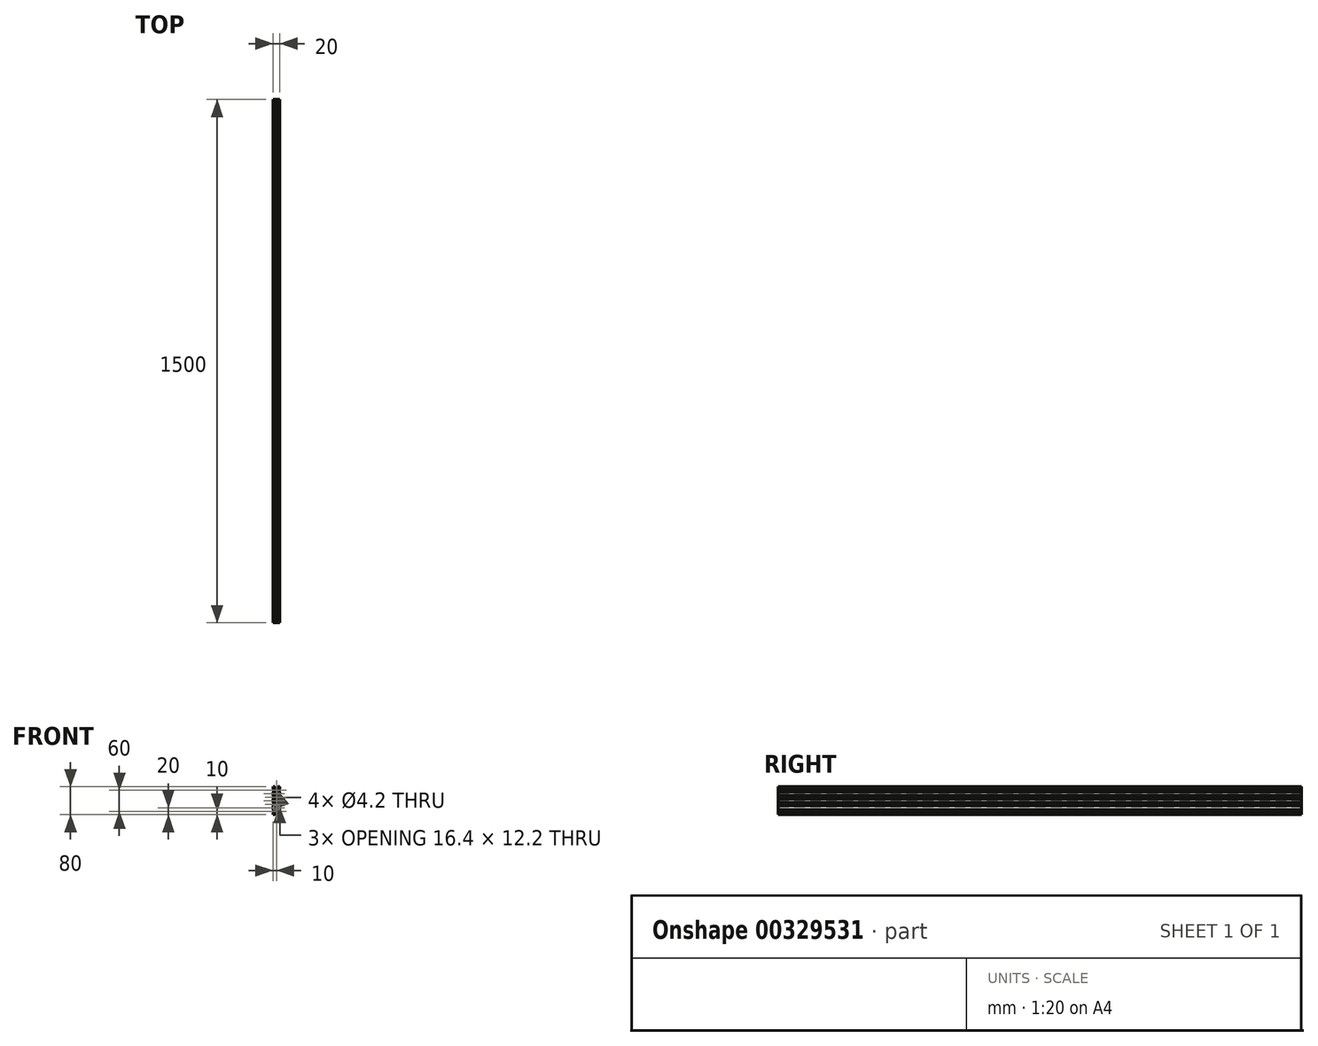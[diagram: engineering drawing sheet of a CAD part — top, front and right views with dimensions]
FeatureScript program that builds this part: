
annotation { "Feature Type Name" : "Feature", "Feature Type Description" : "" }
export const myFeature = defineFeature(function(context is Context, id is Id, definition is map)
    precondition{}
    {
        {
            var Q0;
            Q0=qCreatedBy(makeId("Front.planeOp"),FACE);
            var sketch = newSketch(context, id + "F0", { "sketchPlane" : qUnion([Q0])});
            skCircle(sketch, "E0", {"center": v(0, -30) * mm, "radius": 2.1 * mm});
            skCircle(sketch, "E1", {"center": v(0, -10) * mm, "radius": 2.1 * mm});
            skCircle(sketch, "E2", {"center": v(0, 10) * mm, "radius": 2.1 * mm});
            skCircle(sketch, "E3", {"center": v(0, 30) * mm, "radius": 2.1 * mm});
            skLineSegment(sketch, "E4.bottom", {"start": v(-10, 40) * mm, "end": v(-4.58, 40) * mm});
            skLineSegment(sketch, "E4.top", {"start": v(-10, -40) * mm, "end": v(-4.58, -40) * mm});
            skLineSegment(sketch, "E4.left", {"start": v(-10, 40) * mm, "end": v(-10, 34.58) * mm});
            skLineSegment(sketch, "E4.right", {"start": v(10, 40) * mm, "end": v(10, 34.58) * mm});
            skLineSegment(sketch, "E5", {"start": v(4.58, 40) * mm, "end": v(3.13, 38.2) * mm});
            skLineSegment(sketch, "E6", {"start": v(3.12, 38.2) * mm, "end": v(5.5, 38.2) * mm});
            skLineSegment(sketch, "E7", {"start": v(5.5, 38.2) * mm, "end": v(5.5, 36.56) * mm});
            skLineSegment(sketch, "E8", {"start": v(5.5, 36.56) * mm, "end": v(2.84, 33.9) * mm});
            skLineSegment(sketch, "E9", {"start": v(2.84, 33.9) * mm, "end": v(-2.84, 33.9) * mm});
            skLineSegment(sketch, "E10", {"start": v(-2.84, 33.9) * mm, "end": v(-5.5, 36.56) * mm});
            skLineSegment(sketch, "E11", {"start": v(-5.5, 36.56) * mm, "end": v(-5.5, 38.2) * mm});
            skLineSegment(sketch, "E12", {"start": v(-5.5, 38.2) * mm, "end": v(-3.12, 38.2) * mm});
            skLineSegment(sketch, "E13", {"start": v(-3.13, 38.2) * mm, "end": v(-4.58, 40) * mm});
            skLineSegment(sketch, "E14", {"start": v(0, 30) * mm, "end": v(-10, 40) * mm, "construction": true});
            skLineSegment(sketch, "E15", {"start": v(0, 30) * mm, "end": v(10, 40) * mm, "construction": true});
            skLineSegment(sketch, "E16.trimOffspring", {"start": v(4.58, 40) * mm, "end": v(10, 40) * mm});
            skLineSegment(sketch, "E17", {"start": v(-10, 34.58) * mm, "end": v(-8.2, 33.12) * mm});
            skLineSegment(sketch, "E18", {"start": v(-8.2, 33.12) * mm, "end": v(-8.2, 35.5) * mm});
            skLineSegment(sketch, "E19", {"start": v(-3.9, 32.84) * mm, "end": v(-3.9, 27.16) * mm});
            skLineSegment(sketch, "E20", {"start": v(-8.2, 24.5) * mm, "end": v(-8.2, 26.87) * mm});
            skLineSegment(sketch, "E21", {"start": v(-8.2, 26.88) * mm, "end": v(-10, 25.42) * mm});
            skLineSegment(sketch, "E22", {"start": v(-8.2, 35.5) * mm, "end": v(-6.56, 35.5) * mm});
            skLineSegment(sketch, "E23", {"start": v(-6.56, 35.5) * mm, "end": v(-3.9, 32.84) * mm});
            skLineSegment(sketch, "E24", {"start": v(-3.9, 27.16) * mm, "end": v(-6.56, 24.5) * mm});
            skLineSegment(sketch, "E25", {"start": v(-6.56, 24.5) * mm, "end": v(-8.2, 24.5) * mm});
            skPoint(sketch, "E26", {"position": v(-3.9, 30) * mm});
            skLineSegment(sketch, "E27.trimOffspring", {"start": v(-10, 25.42) * mm, "end": v(-10, 14.58) * mm});
            skLineSegment(sketch, "E28.0.1.0", {"start": v(-10, 14.58) * mm, "end": v(-8.2, 13.13) * mm});
            skLineSegment(sketch, "E28.0.1.1", {"start": v(-8.2, 13.13) * mm, "end": v(-8.2, 15.5) * mm});
            skLineSegment(sketch, "E28.0.1.2", {"start": v(-8.2, 15.5) * mm, "end": v(-6.56, 15.5) * mm});
            skLineSegment(sketch, "E28.0.1.3", {"start": v(-6.56, 15.5) * mm, "end": v(-3.9, 12.84) * mm});
            skLineSegment(sketch, "E28.0.1.4", {"start": v(-3.9, 12.84) * mm, "end": v(-3.9, 7.16) * mm});
            skLineSegment(sketch, "E28.0.1.5", {"start": v(-3.9, 7.16) * mm, "end": v(-6.56, 4.5) * mm});
            skLineSegment(sketch, "E28.0.1.6", {"start": v(-6.56, 4.5) * mm, "end": v(-8.2, 4.5) * mm});
            skLineSegment(sketch, "E28.0.1.7", {"start": v(-8.2, 4.5) * mm, "end": v(-8.2, 6.88) * mm});
            skLineSegment(sketch, "E28.0.1.8", {"start": v(-8.2, 6.88) * mm, "end": v(-10, 5.42) * mm});
            skLineSegment(sketch, "E28.0.2.0", {"start": v(-10, -5.42) * mm, "end": v(-8.2, -6.87) * mm});
            skLineSegment(sketch, "E28.0.2.1", {"start": v(-8.2, -6.87) * mm, "end": v(-8.2, -4.5) * mm});
            skLineSegment(sketch, "E28.0.2.2", {"start": v(-8.2, -4.5) * mm, "end": v(-6.56, -4.5) * mm});
            skLineSegment(sketch, "E28.0.2.3", {"start": v(-6.56, -4.5) * mm, "end": v(-3.9, -7.16) * mm});
            skLineSegment(sketch, "E28.0.2.4", {"start": v(-3.9, -7.16) * mm, "end": v(-3.9, -12.84) * mm});
            skLineSegment(sketch, "E28.0.2.5", {"start": v(-3.9, -12.84) * mm, "end": v(-6.56, -15.5) * mm});
            skLineSegment(sketch, "E28.0.2.6", {"start": v(-6.56, -15.5) * mm, "end": v(-8.2, -15.5) * mm});
            skLineSegment(sketch, "E28.0.2.7", {"start": v(-8.2, -15.5) * mm, "end": v(-8.2, -13.12) * mm});
            skLineSegment(sketch, "E28.0.2.8", {"start": v(-8.2, -13.12) * mm, "end": v(-10, -14.58) * mm});
            skLineSegment(sketch, "E28.0.3.0", {"start": v(-10, -25.42) * mm, "end": v(-8.2, -26.87) * mm});
            skLineSegment(sketch, "E28.0.3.1", {"start": v(-8.2, -26.87) * mm, "end": v(-8.2, -24.5) * mm});
            skLineSegment(sketch, "E28.0.3.2", {"start": v(-8.2, -24.5) * mm, "end": v(-6.56, -24.5) * mm});
            skLineSegment(sketch, "E28.0.3.3", {"start": v(-6.56, -24.5) * mm, "end": v(-3.9, -27.16) * mm});
            skLineSegment(sketch, "E28.0.3.4", {"start": v(-3.9, -27.16) * mm, "end": v(-3.9, -32.84) * mm});
            skLineSegment(sketch, "E28.0.3.5", {"start": v(-3.9, -32.84) * mm, "end": v(-6.56, -35.5) * mm});
            skLineSegment(sketch, "E28.0.3.6", {"start": v(-6.56, -35.5) * mm, "end": v(-8.2, -35.5) * mm});
            skLineSegment(sketch, "E28.0.3.7", {"start": v(-8.2, -35.5) * mm, "end": v(-8.2, -33.12) * mm});
            skLineSegment(sketch, "E28.0.3.8", {"start": v(-8.2, -33.12) * mm, "end": v(-10, -34.58) * mm});
            skLineSegment(sketch, "E28.direction1", {"start": v(-10, 34.58) * mm, "end": v(-10, 34.58) * mm});
            skLineSegment(sketch, "E28.direction2", {"start": v(-10, 34.58) * mm, "end": v(-10, 14.58) * mm, "construction": true});
            skLineSegment(sketch, "E29.trimOffspring", {"start": v(-10, 5.42) * mm, "end": v(-10, -5.42) * mm});
            skLineSegment(sketch, "E30.trimOffspring", {"start": v(-10, -14.58) * mm, "end": v(-10, -25.42) * mm});
            skLineSegment(sketch, "E31.trimOffspring", {"start": v(-10, -34.58) * mm, "end": v(-10, -40) * mm});
            skLineSegment(sketch, "E32", {"start": v(10, -25.42) * mm, "end": v(8.2, -26.87) * mm});
            skLineSegment(sketch, "E33", {"start": v(8.2, -26.87) * mm, "end": v(8.2, -24.5) * mm});
            skLineSegment(sketch, "E34", {"start": v(8.2, -24.5) * mm, "end": v(6.56, -24.5) * mm});
            skLineSegment(sketch, "E35", {"start": v(6.56, -24.5) * mm, "end": v(3.9, -27.16) * mm});
            skLineSegment(sketch, "E36", {"start": v(3.9, -27.16) * mm, "end": v(3.9, -32.84) * mm});
            skLineSegment(sketch, "E37", {"start": v(3.9, -32.84) * mm, "end": v(6.56, -35.5) * mm});
            skLineSegment(sketch, "E38", {"start": v(6.56, -35.5) * mm, "end": v(8.2, -35.5) * mm});
            skLineSegment(sketch, "E39", {"start": v(8.2, -35.5) * mm, "end": v(8.2, -33.12) * mm});
            skLineSegment(sketch, "E40", {"start": v(8.2, -33.12) * mm, "end": v(10, -34.58) * mm});
            skLineSegment(sketch, "E41.trimOffspring", {"start": v(10, -34.58) * mm, "end": v(10, -40) * mm});
            skLineSegment(sketch, "E42", {"start": v(-4.58, -40) * mm, "end": v(-3.12, -38.2) * mm});
            skLineSegment(sketch, "E43", {"start": v(-3.12, -38.2) * mm, "end": v(-5.5, -38.2) * mm});
            skLineSegment(sketch, "E44", {"start": v(-5.5, -38.2) * mm, "end": v(-5.5, -36.56) * mm});
            skLineSegment(sketch, "E45", {"start": v(-5.5, -36.56) * mm, "end": v(-2.84, -33.9) * mm});
            skLineSegment(sketch, "E46", {"start": v(-2.84, -33.9) * mm, "end": v(2.84, -33.9) * mm});
            skLineSegment(sketch, "E47", {"start": v(2.84, -33.9) * mm, "end": v(5.5, -36.56) * mm});
            skLineSegment(sketch, "E48", {"start": v(5.5, -36.56) * mm, "end": v(5.5, -38.2) * mm});
            skLineSegment(sketch, "E49", {"start": v(5.5, -38.2) * mm, "end": v(3.13, -38.2) * mm});
            skLineSegment(sketch, "E50", {"start": v(3.13, -38.2) * mm, "end": v(4.58, -40) * mm});
            skLineSegment(sketch, "E51.trimOffspring", {"start": v(4.58, -40) * mm, "end": v(10, -40) * mm});
            skLineSegment(sketch, "E52.0.1.0", {"start": v(10, -5.42) * mm, "end": v(8.2, -6.87) * mm});
            skLineSegment(sketch, "E52.0.1.1", {"start": v(8.2, -6.87) * mm, "end": v(8.2, -4.5) * mm});
            skLineSegment(sketch, "E52.0.1.2", {"start": v(8.2, -4.5) * mm, "end": v(6.56, -4.5) * mm});
            skLineSegment(sketch, "E52.0.1.3", {"start": v(6.56, -4.5) * mm, "end": v(3.9, -7.16) * mm});
            skLineSegment(sketch, "E52.0.1.4", {"start": v(3.9, -7.16) * mm, "end": v(3.9, -12.84) * mm});
            skLineSegment(sketch, "E52.0.1.5", {"start": v(3.9, -12.84) * mm, "end": v(6.56, -15.5) * mm});
            skLineSegment(sketch, "E52.0.1.6", {"start": v(6.56, -15.5) * mm, "end": v(8.2, -15.5) * mm});
            skLineSegment(sketch, "E52.0.1.7", {"start": v(8.2, -15.5) * mm, "end": v(8.2, -13.12) * mm});
            skLineSegment(sketch, "E52.0.1.8", {"start": v(8.2, -13.12) * mm, "end": v(10, -14.58) * mm});
            skLineSegment(sketch, "E52.0.2.0", {"start": v(10, 14.58) * mm, "end": v(8.2, 13.13) * mm});
            skLineSegment(sketch, "E52.0.2.1", {"start": v(8.2, 13.13) * mm, "end": v(8.2, 15.5) * mm});
            skLineSegment(sketch, "E52.0.2.2", {"start": v(8.2, 15.5) * mm, "end": v(6.56, 15.5) * mm});
            skLineSegment(sketch, "E52.0.2.3", {"start": v(6.56, 15.5) * mm, "end": v(3.9, 12.84) * mm});
            skLineSegment(sketch, "E52.0.2.4", {"start": v(3.9, 12.84) * mm, "end": v(3.9, 7.16) * mm});
            skLineSegment(sketch, "E52.0.2.5", {"start": v(3.9, 7.16) * mm, "end": v(6.56, 4.5) * mm});
            skLineSegment(sketch, "E52.0.2.6", {"start": v(6.56, 4.5) * mm, "end": v(8.2, 4.5) * mm});
            skLineSegment(sketch, "E52.0.2.7", {"start": v(8.2, 4.5) * mm, "end": v(8.2, 6.88) * mm});
            skLineSegment(sketch, "E52.0.2.8", {"start": v(8.2, 6.88) * mm, "end": v(10, 5.42) * mm});
            skLineSegment(sketch, "E52.0.3.0", {"start": v(10, 34.58) * mm, "end": v(8.2, 33.13) * mm});
            skLineSegment(sketch, "E52.0.3.1", {"start": v(8.2, 33.13) * mm, "end": v(8.2, 35.5) * mm});
            skLineSegment(sketch, "E52.0.3.2", {"start": v(8.2, 35.5) * mm, "end": v(6.56, 35.5) * mm});
            skLineSegment(sketch, "E52.0.3.3", {"start": v(6.56, 35.5) * mm, "end": v(3.9, 32.84) * mm});
            skLineSegment(sketch, "E52.0.3.4", {"start": v(3.9, 32.84) * mm, "end": v(3.9, 27.16) * mm});
            skLineSegment(sketch, "E52.0.3.5", {"start": v(3.9, 27.16) * mm, "end": v(6.56, 24.5) * mm});
            skLineSegment(sketch, "E52.0.3.6", {"start": v(6.56, 24.5) * mm, "end": v(8.2, 24.5) * mm});
            skLineSegment(sketch, "E52.0.3.7", {"start": v(8.2, 24.5) * mm, "end": v(8.2, 26.88) * mm});
            skLineSegment(sketch, "E52.0.3.8", {"start": v(8.2, 26.88) * mm, "end": v(10, 25.42) * mm});
            skLineSegment(sketch, "E52.direction1", {"start": v(8.2, -26.87) * mm, "end": v(8.2, -26.87) * mm});
            skLineSegment(sketch, "E52.direction2", {"start": v(8.2, -26.87) * mm, "end": v(8.2, -6.87) * mm, "construction": true});
            skLineSegment(sketch, "E53.trimOffspring", {"start": v(10, -14.58) * mm, "end": v(10, -25.42) * mm});
            skLineSegment(sketch, "E54.trimOffspring", {"start": v(10, 5.42) * mm, "end": v(10, -5.42) * mm});
            skLineSegment(sketch, "E55.trimOffspring", {"start": v(10, 25.42) * mm, "end": v(10, 14.58) * mm});
            skLineSegment(sketch, "E56", {"start": v(-2.84, 26.1) * mm, "end": v(2.84, 26.1) * mm});
            skLineSegment(sketch, "E57", {"start": v(2.84, 26.1) * mm, "end": v(5.94, 23) * mm});
            skLineSegment(sketch, "E58", {"start": v(5.94, 23) * mm, "end": v(8.2, 23) * mm});
            skLineSegment(sketch, "E59", {"start": v(8.2, 23) * mm, "end": v(8.2, 17) * mm});
            skLineSegment(sketch, "E60", {"start": v(8.2, 17) * mm, "end": v(5.94, 17) * mm});
            skLineSegment(sketch, "E61", {"start": v(5.94, 17) * mm, "end": v(2.84, 13.9) * mm});
            skLineSegment(sketch, "E62", {"start": v(2.84, 13.9) * mm, "end": v(-2.84, 13.9) * mm});
            skLineSegment(sketch, "E63", {"start": v(-2.84, 13.9) * mm, "end": v(-5.94, 17) * mm});
            skLineSegment(sketch, "E64", {"start": v(-5.94, 17) * mm, "end": v(-8.2, 17) * mm});
            skLineSegment(sketch, "E65", {"start": v(-8.2, 17) * mm, "end": v(-8.2, 23) * mm});
            skLineSegment(sketch, "E66", {"start": v(-8.2, 23) * mm, "end": v(-5.94, 23) * mm});
            skLineSegment(sketch, "E67", {"start": v(-5.94, 23) * mm, "end": v(-2.84, 26.1) * mm});
            skLineSegment(sketch, "E68.0.1.0", {"start": v(-2.84, 6.1) * mm, "end": v(2.84, 6.1) * mm});
            skLineSegment(sketch, "E68.0.1.1", {"start": v(-5.94, 3) * mm, "end": v(-2.84, 6.1) * mm});
            skLineSegment(sketch, "E68.0.1.2", {"start": v(-8.2, 3) * mm, "end": v(-5.94, 3) * mm});
            skLineSegment(sketch, "E68.0.1.3", {"start": v(-8.2, -3) * mm, "end": v(-8.2, 3) * mm});
            skLineSegment(sketch, "E68.0.1.4", {"start": v(-5.94, -3) * mm, "end": v(-8.2, -3) * mm});
            skLineSegment(sketch, "E68.0.1.5", {"start": v(-2.84, -6.1) * mm, "end": v(-5.94, -3) * mm});
            skLineSegment(sketch, "E68.0.1.6", {"start": v(2.84, -6.1) * mm, "end": v(-2.84, -6.1) * mm});
            skLineSegment(sketch, "E68.0.1.7", {"start": v(5.94, -3) * mm, "end": v(2.84, -6.1) * mm});
            skLineSegment(sketch, "E68.0.1.8", {"start": v(8.2, -3) * mm, "end": v(5.94, -3) * mm});
            skLineSegment(sketch, "E68.0.1.9", {"start": v(8.2, 3) * mm, "end": v(8.2, -3) * mm});
            skLineSegment(sketch, "E68.0.1.10", {"start": v(5.94, 3) * mm, "end": v(8.2, 3) * mm});
            skLineSegment(sketch, "E68.0.1.11", {"start": v(2.84, 6.1) * mm, "end": v(5.94, 3) * mm});
            skLineSegment(sketch, "E68.0.2.0", {"start": v(-2.84, -13.9) * mm, "end": v(2.84, -13.9) * mm});
            skLineSegment(sketch, "E68.0.2.1", {"start": v(-5.94, -17) * mm, "end": v(-2.84, -13.9) * mm});
            skLineSegment(sketch, "E68.0.2.2", {"start": v(-8.2, -17) * mm, "end": v(-5.94, -17) * mm});
            skLineSegment(sketch, "E68.0.2.3", {"start": v(-8.2, -23) * mm, "end": v(-8.2, -17) * mm});
            skLineSegment(sketch, "E68.0.2.4", {"start": v(-5.94, -23) * mm, "end": v(-8.2, -23) * mm});
            skLineSegment(sketch, "E68.0.2.5", {"start": v(-2.84, -26.1) * mm, "end": v(-5.94, -23) * mm});
            skLineSegment(sketch, "E68.0.2.6", {"start": v(2.84, -26.1) * mm, "end": v(-2.84, -26.1) * mm});
            skLineSegment(sketch, "E68.0.2.7", {"start": v(5.94, -23) * mm, "end": v(2.84, -26.1) * mm});
            skLineSegment(sketch, "E68.0.2.8", {"start": v(8.2, -23) * mm, "end": v(5.94, -23) * mm});
            skLineSegment(sketch, "E68.0.2.9", {"start": v(8.2, -17) * mm, "end": v(8.2, -23) * mm});
            skLineSegment(sketch, "E68.0.2.10", {"start": v(5.94, -17) * mm, "end": v(8.2, -17) * mm});
            skLineSegment(sketch, "E68.0.2.11", {"start": v(2.84, -13.9) * mm, "end": v(5.94, -17) * mm});
            skLineSegment(sketch, "E68.direction1", {"start": v(-2.84, 26.1) * mm, "end": v(22.16, 26.1) * mm, "construction": true});
            skLineSegment(sketch, "E68.direction2", {"start": v(-2.84, 26.1) * mm, "end": v(-2.84, 6.1) * mm, "construction": true});
            skSolve(sketch);
        }
        {
            var Q0;
            Q0 = qSketchRegion(id + "F0", true);
            extrude(context, id + "F1", {"entities" : qUnion([Q0]), "endBound" : BoundingType.SYMMETRIC, "depth" : 1500 * mm});
        }
    });
